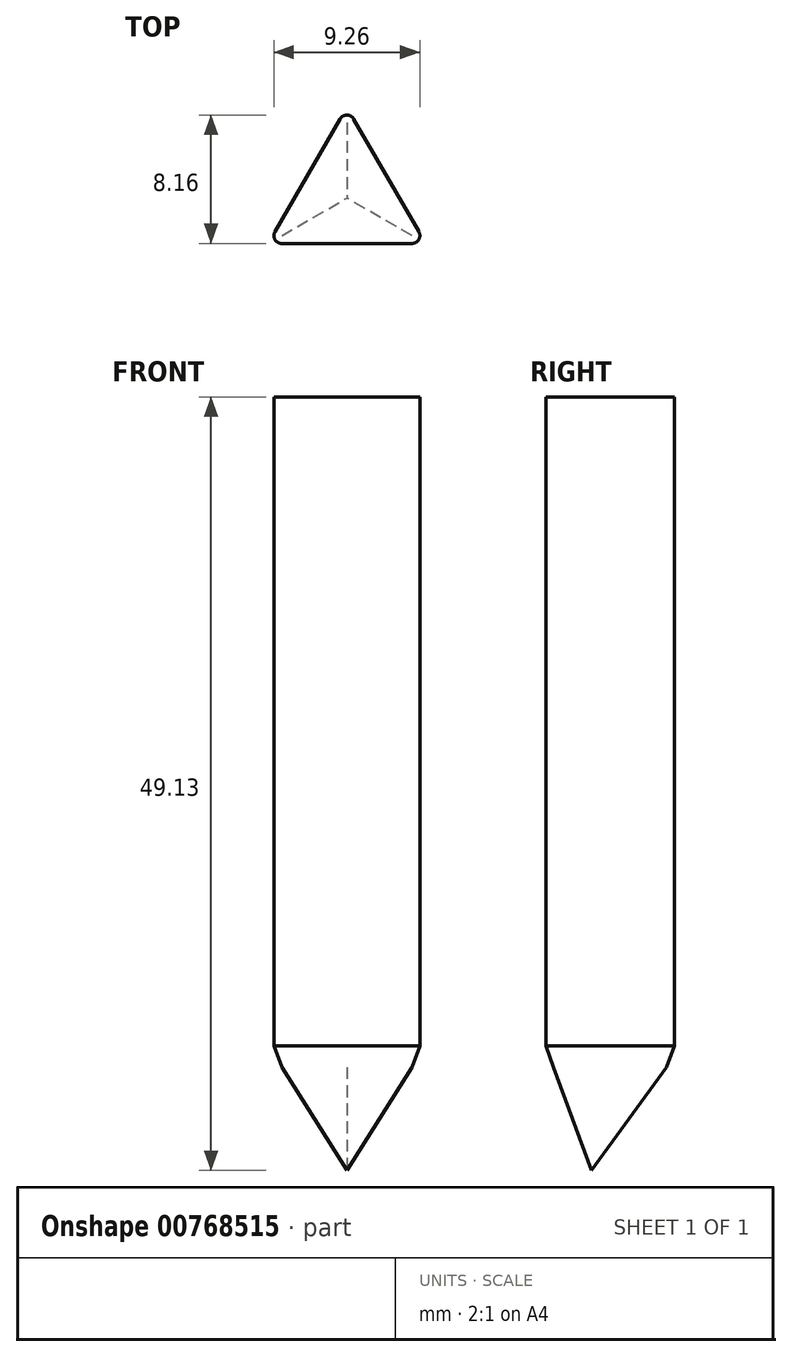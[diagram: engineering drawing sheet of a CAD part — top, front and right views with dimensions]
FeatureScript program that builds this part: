
annotation { "Feature Type Name" : "Feature", "Feature Type Description" : "" }
export const myFeature = defineFeature(function(context is Context, id is Id, definition is map)
    precondition{}
    {
        {
            var Q0;
            Q0=qCreatedBy(makeId("Top.planeOp"),FACE);
            var sketch = newSketch(context, id + "F0", { "sketchPlane" : qUnion([Q0])});
            skCircle(sketch, "E0.cCircle", {"center": v(0, 0) * mm, "radius": 5.77 * mm, "construction": true});
            skLineSegment(sketch, "E0.0", {"start": v(0.43, 5.02) * mm, "end": v(4.57, -2.14) * mm});
            skLineSegment(sketch, "E0.1", {"start": v(4.13, -2.89) * mm, "end": v(-4.13, -2.89) * mm});
            skLineSegment(sketch, "E0.2", {"start": v(-4.57, -2.14) * mm, "end": v(-0.43, 5.02) * mm});
            skPoint(sketch, "E1.visualSharp", {"position": v(0, 5.77) * mm});
            skArc(sketch, "E1.filletArc", {"start": v(0.43, 5.02) * mm, "mid": v(0, 5.27) * mm, "end": v(-0.43, 5.02) * mm});
            skPoint(sketch, "E2.visualSharp", {"position": v(5, -2.89) * mm});
            skArc(sketch, "E2.filletArc", {"start": v(4.13, -2.89) * mm, "mid": v(4.57, -2.64) * mm, "end": v(4.57, -2.14) * mm});
            skPoint(sketch, "E3.visualSharp", {"position": v(-5, -2.89) * mm});
            skArc(sketch, "E3.filletArc", {"start": v(-4.57, -2.14) * mm, "mid": v(-4.57, -2.64) * mm, "end": v(-4.13, -2.89) * mm});
            skSolve(sketch);
        }
        {
            var Q0;
            Q0=makeQuery(id+"F0.imprint","IMPRINT",FACE,{"disambiguationData":[TD([[makeQuery(id+"F0.imprint","IMPRINT",EDGE,{"derivedFrom":sQuery(id+"F0.wireOp",EDGE,"E0.0")}),-1.0]])]});
            extrude(context, id + "F1", {"entities" : qUnion([Q0]), "depth" : 41.2 * mm, "offsetDistance" : 25 * mm, "hasSecondDirection" : true, "secondDirectionOppositeDirection" : true, "secondDirectionDepth" : 25 * mm, "hasSecondDirectionDraft" : true, "secondDirectionDraftAngle" : 20 * degree, "secondDirectionDraftPullDirection" : true});
        }
    });
